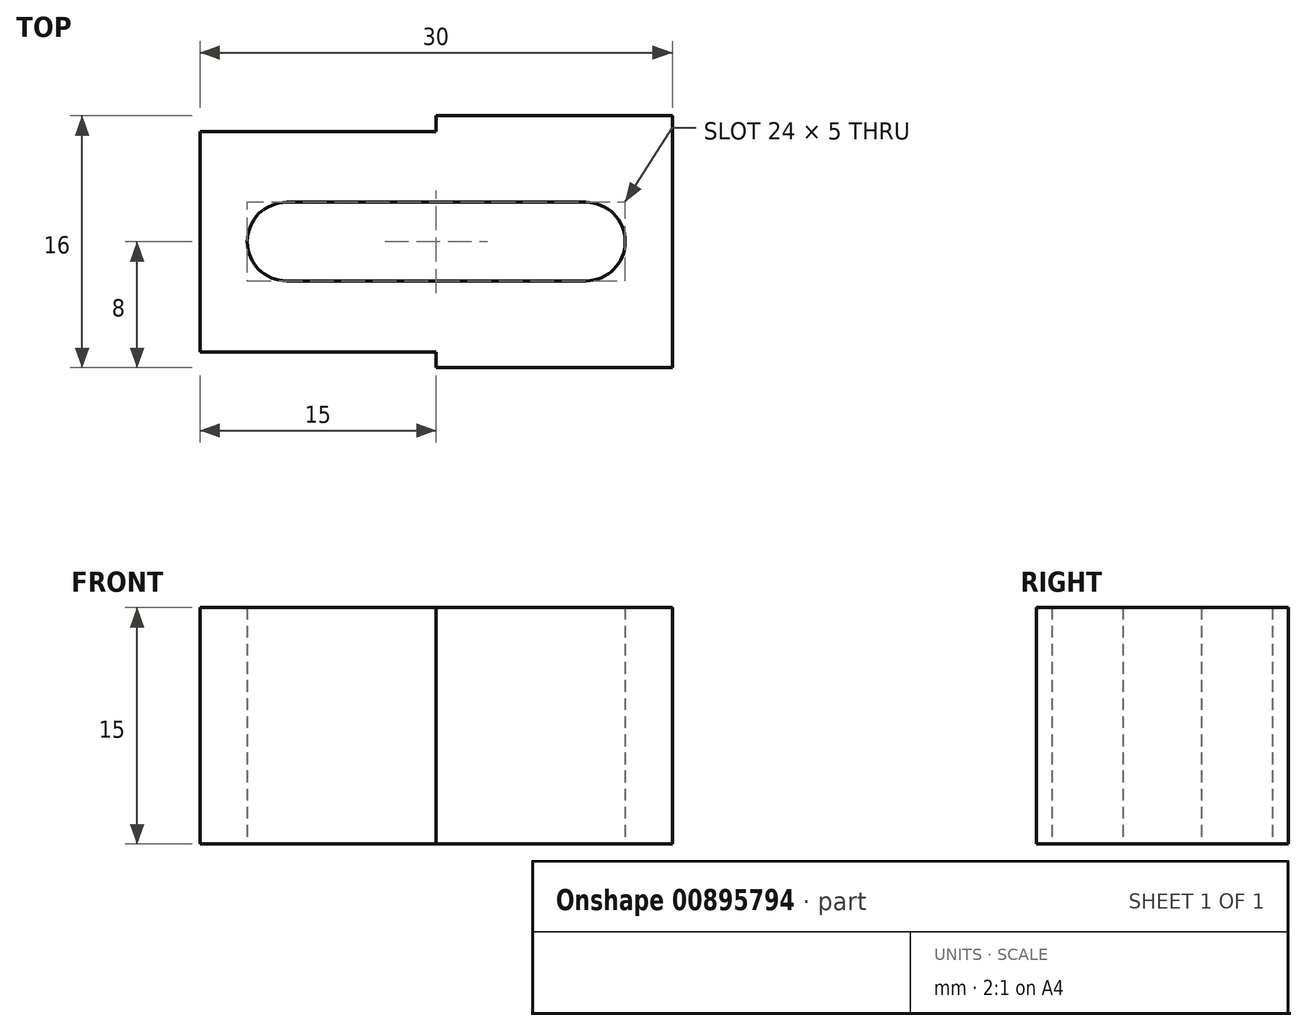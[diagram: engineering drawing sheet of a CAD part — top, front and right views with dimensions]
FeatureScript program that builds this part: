
annotation { "Feature Type Name" : "Feature", "Feature Type Description" : "" }
export const myFeature = defineFeature(function(context is Context, id is Id, definition is map)
    precondition{}
    {
        {
            var Q0;
            Q0=qCreatedBy(makeId("Top.planeOp"),FACE);
            var sketch = newSketch(context, id + "F0", { "sketchPlane" : qUnion([Q0])});
            skLineSegment(sketch, "E0.bottom", {"start": v(-15, 7) * mm, "end": v(0, 7) * mm});
            skLineSegment(sketch, "E0.top", {"start": v(-15, -7) * mm, "end": v(0, -7) * mm});
            skPoint(sketch, "E0.middle", {"position": v(0, 0) * mm});
            skLineSegment(sketch, "E1.bottom", {"start": v(-9.5, 2.5) * mm, "end": v(9.5, 2.5) * mm});
            skLineSegment(sketch, "E1.top", {"start": v(-9.5, -2.5) * mm, "end": v(9.5, -2.5) * mm});
            skLineSegment(sketch, "E1.left", {"start": v(-12, 0) * mm, "end": v(-12, 0) * mm});
            skLineSegment(sketch, "E1.right", {"start": v(12, 0) * mm, "end": v(12, 0) * mm});
            skPoint(sketch, "E2.visualSharp", {"position": v(-12, 2.5) * mm});
            skArc(sketch, "E2.filletArc", {"start": v(-9.5, 2.5) * mm, "mid": v(-11.27, 1.77) * mm, "end": v(-12, 0) * mm});
            skPoint(sketch, "E3.visualSharp", {"position": v(-12, -2.5) * mm});
            skArc(sketch, "E3.filletArc", {"start": v(-12, 0) * mm, "mid": v(-11.27, -1.77) * mm, "end": v(-9.5, -2.5) * mm});
            skPoint(sketch, "E4.visualSharp", {"position": v(12, 2.5) * mm});
            skArc(sketch, "E4.filletArc", {"start": v(12, 0) * mm, "mid": v(11.27, 1.77) * mm, "end": v(9.5, 2.5) * mm});
            skPoint(sketch, "E5.visualSharp", {"position": v(12, -2.5) * mm});
            skArc(sketch, "E5.filletArc", {"start": v(9.5, -2.5) * mm, "mid": v(11.27, -1.77) * mm, "end": v(12, 0) * mm});
            skLineSegment(sketch, "E6", {"start": v(0, 7) * mm, "end": v(0, 8) * mm});
            skLineSegment(sketch, "E7", {"start": v(0, 8) * mm, "end": v(15, 8) * mm});
            skLineSegment(sketch, "E8", {"start": v(15, -8) * mm, "end": v(0, -8) * mm});
            skLineSegment(sketch, "E9", {"start": v(0, -8) * mm, "end": v(0, -7) * mm});
            skLineSegment(sketch, "E10", {"start": v(-15, 7) * mm, "end": v(-15, -7) * mm});
            skLineSegment(sketch, "E11", {"start": v(15, 8) * mm, "end": v(15, -8) * mm});
            skSolve(sketch);
        }
        {
            var Q0;
            Q0=qSketchRegion(id+"F0",true);
            extrude(context, id + "F1", {"entities" : qUnion([Q0]), "depth" : 15 * mm, "offsetDistance" : 25 * mm});
        }
    });
